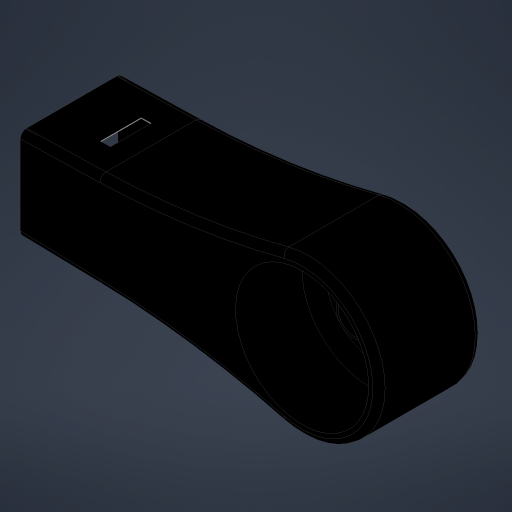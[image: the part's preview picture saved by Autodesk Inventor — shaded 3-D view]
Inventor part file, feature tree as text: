
AUTODESK INVENTOR PART (.ipt)
format: ipt  version: 2023 (Build 270158000, 158)  size: 299,520 bytes
history: native  units: mm
features: extrude x6, sketch x6, fillet x5, chamfer x1
ambient origin geometry x8: Origin, YZ Plane, XZ Plane, XY Plane, X Axis, Y Axis, Z Axis, Center Point
bodies: Solid1 (feature_tree)
feature tree (18):
  extrude  "Extrusion1"  Depth=50.0mm TaperAngle=0.0deg
  extrude  "Extrusion2"  Depth=40.0mm TaperAngle=0.0deg
  extrude  "Extrusion3"  Depth=17.0mm
  chamfer  "Chamfer1"  Distance=15.0mm
  fillet  "Fillet1"  Radius=10.0mm
  fillet  "Fillet2"  Radius=5.0mm
  fillet  "Fillet5"  Radius=100.0mm
  fillet  "Fillet6"  Radius=22.5mm
  extrude  "Extrusion5"  Depth=37.5mm
  extrude  "Extrusion6"  Depth=400.0mm
  fillet  "Fillet7"  Radius=3.0mm
  extrude  "Extrusion8"  Depth=20.0mm
  sketch  "Sketch1"  dims[d0=75.0mm d1=50.0mm d2=0.0mm]
  sketch  "Sketch2"  dims[d3=65.0mm d4=40.0mm d5=0.0mm]
  sketch  "Sketch3"  dims[d6=15.0mm d7=17.0mm d8=15.0mm d9=0.0mm]
  sketch  "Sketch5"  dims[d10=24.0mm d11=10.0mm d12=45.0deg d13=10.0mm d14=5.0mm d15=100.0mm d16=22.5mm]
  sketch  "Sketch6"  dims[d17=45.0mm d18=37.5mm]
  sketch  "Sketch8"  dims[d19=135.0deg d27=400.0mm d28=3.0mm d29=2.5mm d30=45.0mm d31=90.0deg d32=45.0mm d33=90.0deg d34=45.0mm d35=35.0mm d36=0.0mm d37=50.0mm d38=5.0mm d39=0.0mm d40=2.0mm d47=6.0mm d48=10.0mm d49=5.0mm d50=20.0mm d51=6.0mm d52=0.0mm d22=0.0mm d23=0.0mm d24=0.0mm d25=0.0mm]
